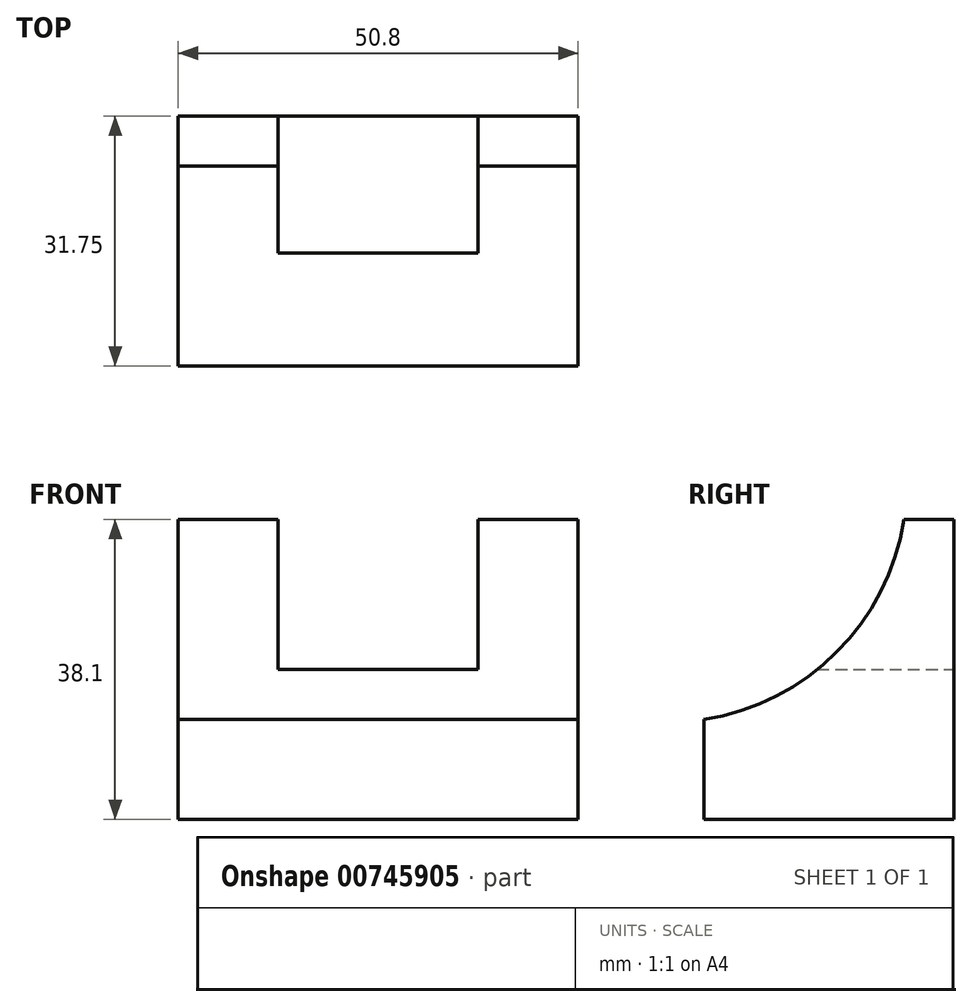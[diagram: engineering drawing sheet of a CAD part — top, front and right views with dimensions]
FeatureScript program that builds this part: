
annotation { "Feature Type Name" : "Feature", "Feature Type Description" : "" }
export const myFeature = defineFeature(function(context is Context, id is Id, definition is map)
    precondition{}
    {
        {
            var Q0;
            Q0=qCreatedBy(makeId("Front.planeOp"),FACE);
            var sketch = newSketch(context, id + "F0", { "sketchPlane" : qUnion([Q0])});
            skLineSegment(sketch, "E0.bottom", {"start": v(0, 0) * mm, "end": v(50.8, 0) * mm});
            skLineSegment(sketch, "E0.top", {"start": v(0, 12.7) * mm, "end": v(50.8, 12.7) * mm});
            skLineSegment(sketch, "E0.left", {"start": v(0, 0) * mm, "end": v(0, 12.7) * mm});
            skLineSegment(sketch, "E0.right", {"start": v(50.8, 0) * mm, "end": v(50.8, 12.7) * mm});
            skSolve(sketch);
        }
        {
            var Q0;
            Q0=makeQuery(id+"F0.imprint","IMPRINT",FACE,{"disambiguationData":[TD([[makeQuery(id+"F0.imprint","IMPRINT",EDGE,{"derivedFrom":sQuery(id+"F0.wireOp",EDGE,"E0.bottom")}),1.0]])]});
            extrude(context, id + "F1", {"entities" : qUnion([Q0]), "oppositeDirection" : true, "depth" : 31.75 * mm, "offsetDistance" : 25.4 * mm});
        }
        {
            var Q0;
            Q0=makeQuery(id+"F1.opExtrude","CAP_FACE",FACE,{"disambiguationData":[OSD([sQuery(id+"F0.wireOp",EDGE,"E0.bottom"),sQuery(id+"F0.wireOp",EDGE,"E0.top"),sQuery(id+"F0.wireOp",EDGE,"E0.left"),sQuery(id+"F0.wireOp",EDGE,"E0.right")])],"isStart":false});
            var sketch = newSketch(context, id + "F2", { "sketchPlane" : qUnion([Q0])});
            skLineSegment(sketch, "E1", {"start": v(-50.8, 12.7) * mm, "end": v(-50.8, 38.1) * mm});
            skLineSegment(sketch, "E2", {"start": v(-50.8, 38.1) * mm, "end": v(-38.1, 38.1) * mm});
            skLineSegment(sketch, "E3", {"start": v(-38.1, 38.1) * mm, "end": v(-38.1, 19.05) * mm});
            skLineSegment(sketch, "E4", {"start": v(-38.1, 19.05) * mm, "end": v(-12.7, 19.05) * mm});
            skLineSegment(sketch, "E5", {"start": v(-12.7, 19.05) * mm, "end": v(-12.7, 38.1) * mm});
            skLineSegment(sketch, "E6", {"start": v(-12.7, 38.1) * mm, "end": v(0, 38.1) * mm});
            skLineSegment(sketch, "E7", {"start": v(0, 38.1) * mm, "end": v(0, 12.7) * mm});
            skSolve(sketch);
        }
        {
            var Q0;
            Q0=makeQuery(id+"F2.imprint","IMPRINT",FACE,{"disambiguationData":[TD([[makeQuery(id+"F2.imprint","IMPRINT",EDGE,{"derivedFrom":sQuery(id+"F2.wireOp",EDGE,"E1")}),-1.0]])]});
            extrude(context, id + "F3", {"entities" : qUnion([Q0]), "operationType" : NewBodyOperationType.ADD, "oppositeDirection" : true, "depth" : 6.35 * mm, "offsetDistance" : 25.4 * mm});
        }
        {
            var Q0;
            Q0=makeQuery(id+"F3.opExtrude","SWEPT_FACE",FACE,{"disambiguationData":[OSD([sQuery(id+"F2.wireOp",EDGE,"E2")])]});
            var sketch = newSketch(context, id + "F4", { "sketchPlane" : qUnion([Q0])});
            skLineSegment(sketch, "E8", {"start": v(50.8, 25.4) * mm, "end": v(50.8, 0) * mm});
            skLineSegment(sketch, "E9", {"start": v(50.8, 0) * mm, "end": v(0, 0) * mm});
            skLineSegment(sketch, "E10", {"start": v(0, 0) * mm, "end": v(0, 25.4) * mm});
            skLineSegment(sketch, "E11", {"start": v(0, 25.4) * mm, "end": v(50.8, 25.4) * mm});
            skSolve(sketch);
        }
        {
            var Q0;
            {var subQ4=sQuery(id+"F4.wireOp",EDGE,"E8");Q0=makeQuery(id+"F4.imprint","IMPRINT",FACE,{"disambiguationData":[TD([[makeQuery(id+"F4.imprint","IMPRINT",EDGE,{"derivedFrom":subQ4}),-1.0]])]});}
            extrude(context, id + "F5", {"entities" : qUnion([Q0]), "operationType" : NewBodyOperationType.ADD, "oppositeDirection" : true, "depth" : 25.4 * mm, "offsetDistance" : 25.4 * mm});
        }
        {
            var Q0;
            Q0=makeQuery(id+"F5.boolean.opBoolean","MERGE",FACE,{"derivedFrom":[makeQuery(id+"F3.boolean.opBoolean","MERGE",FACE,{"derivedFrom":[makeQuery(id+"F1.opExtrude","SWEPT_FACE",FACE,{"disambiguationData":[OSD([sQuery(id+"F0.wireOp",EDGE,"E0.right")])]}),makeQuery(id+"F3.opExtrude","SWEPT_FACE",FACE,{"disambiguationData":[OSD([sQuery(id+"F2.wireOp",EDGE,"E1")])]})]}),makeQuery(id+"F5.opExtrude","SWEPT_FACE",FACE,{"disambiguationData":[OSD([sQuery(id+"F4.wireOp",EDGE,"E8")])]})]});
            var sketch = newSketch(context, id + "F6", { "sketchPlane" : qUnion([Q0])});
            skArc(sketch, "E12", {"start": v(0, 12.7) * mm, "mid": v(16.84, 21.26) * mm, "end": v(25.4, 38.1) * mm});
            skSolve(sketch);
        }
        {
            var Q0;
            {var subQ0=sQuery(id+"F6.wireOp",EDGE,"E12");Q0=makeQuery(id+"F6.imprint","IMPRINT",FACE,{"disambiguationData":[TD([[makeQuery(id+"F6.imprint","IMPRINT",EDGE,{"derivedFrom":subQ0}),1.0]])]});}
            extrude(context, id + "F7", {"entities" : qUnion([Q0]), "operationType" : NewBodyOperationType.REMOVE, "oppositeDirection" : true, "depth" : 50.8 * mm, "offsetDistance" : 25.4 * mm});
        }
        {
            var Q0;
            Q0=makeQuery(id+"F5.opExtrude","SWEPT_FACE",FACE,{"disambiguationData":[OSD([sQuery(id+"F4.wireOp",EDGE,"E11")])]});
            extrude(context, id + "F8", {"entities" : qUnion([Q0]), "operationType" : NewBodyOperationType.REMOVE, "oppositeDirection" : true, "depth" : 25.4 * mm, "offsetDistance" : 25.4 * mm});
        }
    });
